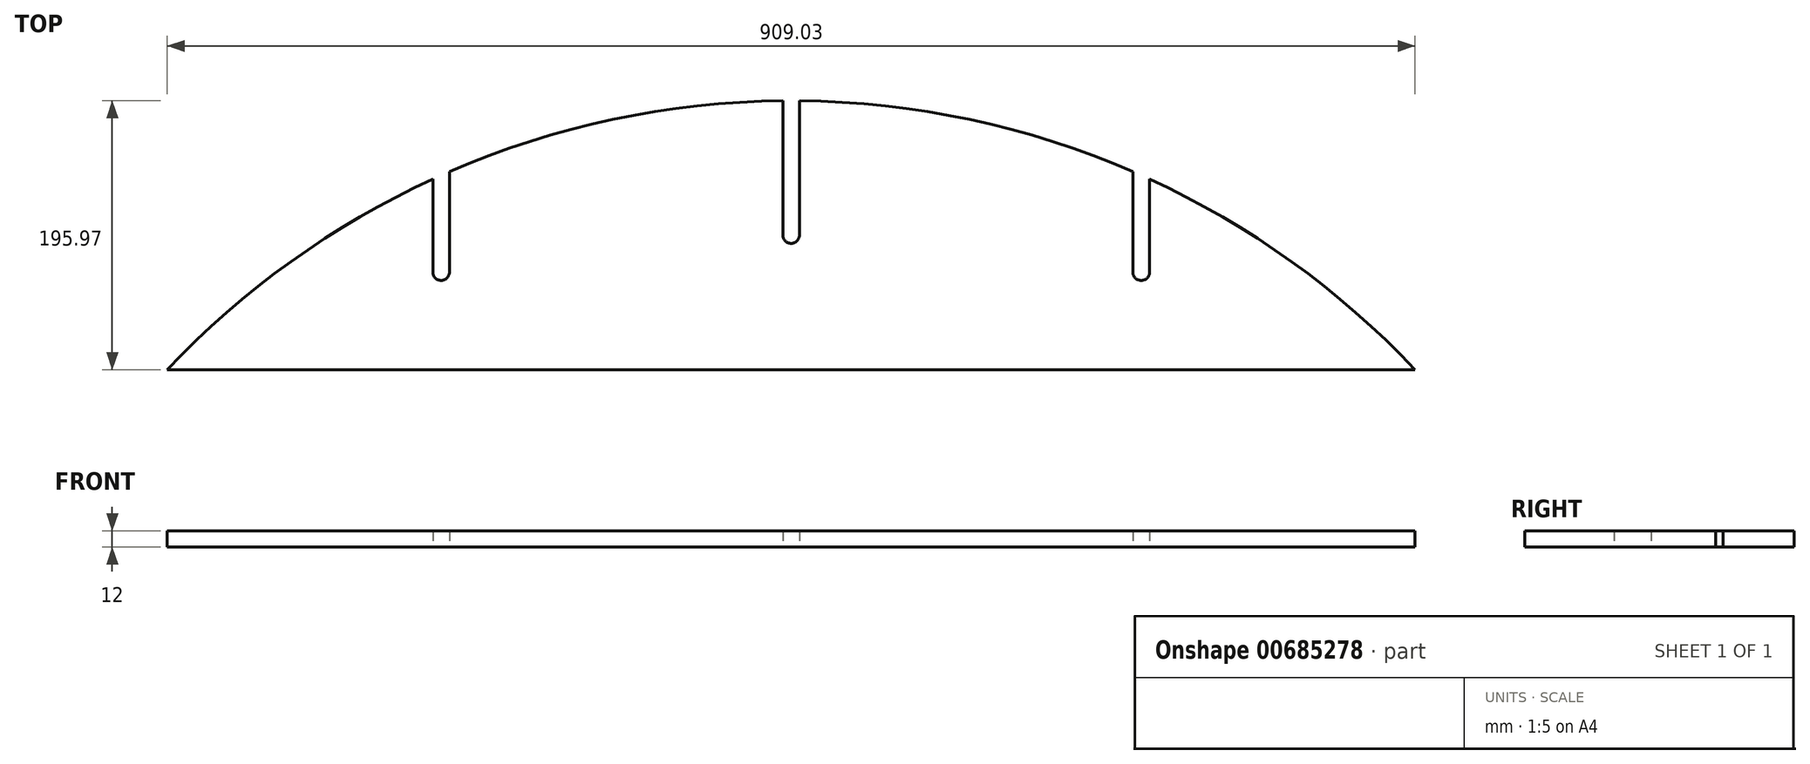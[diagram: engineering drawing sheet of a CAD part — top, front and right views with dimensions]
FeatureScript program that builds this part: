
annotation { "Feature Type Name" : "Feature", "Feature Type Description" : "" }
export const myFeature = defineFeature(function(context is Context, id is Id, definition is map)
    precondition{}
    {
        {
            var Q0;
            Q0=qCreatedBy(makeId("Top.planeOp"),FACE);
            var sketch = newSketch(context, id + "F0", { "sketchPlane" : qUnion([Q0])});
            skArc(sketch, "E0", {"start": v(909.03, 0) * mm, "mid": v(818.95, 78.75) * mm, "end": v(715.52, 138.9) * mm});
            skLineSegment(sketch, "E1", {"start": v(0, 0) * mm, "end": v(909.03, 0) * mm});
            skLineSegment(sketch, "E2", {"start": v(454.52, 252.18) * mm, "end": v(454.52, -138.83) * mm, "construction": true});
            skPoint(sketch, "E3", {"position": v(454.52, 0) * mm});
            skLineSegment(sketch, "E4", {"start": v(448.52, 195.97) * mm, "end": v(448.52, 98) * mm});
            skLineSegment(sketch, "E5", {"start": v(460.52, 98) * mm, "end": v(460.52, 195.97) * mm});
            skArc(sketch, "E6.trimOffspring", {"start": v(448.52, 195.97) * mm, "mid": v(324.42, 182.31) * mm, "end": v(205.52, 144.26) * mm});
            skLineSegment(sketch, "E7", {"start": v(199.52, 141.61) * mm, "end": v(199.52, -61.83) * mm, "construction": true});
            skLineSegment(sketch, "E8", {"start": v(193.52, 138.9) * mm, "end": v(193.52, 71) * mm});
            skLineSegment(sketch, "E9", {"start": v(205.52, 71) * mm, "end": v(205.52, 144.26) * mm});
            skLineSegment(sketch, "E10.MirrorCS", {"start": v(703.52, 71) * mm, "end": v(703.52, 144.26) * mm});
            skLineSegment(sketch, "E11.MirrorCS", {"start": v(715.52, 138.9) * mm, "end": v(715.52, 71) * mm});
            skArc(sketch, "E12.trimOffspring", {"start": v(703.52, 144.26) * mm, "mid": v(584.61, 182.31) * mm, "end": v(460.52, 195.97) * mm});
            skArc(sketch, "E13.trimOffspring", {"start": v(193.52, 138.9) * mm, "mid": v(90.08, 78.75) * mm, "end": v(0, 0) * mm});
            skArc(sketch, "E14", {"start": v(193.52, 71) * mm, "mid": v(199.52, 65) * mm, "end": v(205.52, 71) * mm});
            skArc(sketch, "E15", {"start": v(448.52, 98) * mm, "mid": v(454.52, 92) * mm, "end": v(460.52, 98) * mm});
            skArc(sketch, "E16", {"start": v(703.52, 71) * mm, "mid": v(709.52, 65) * mm, "end": v(715.52, 71) * mm});
            skSolve(sketch);
        }
        {
            var Q0;
            Q0=makeQuery(id+"F0.imprint","IMPRINT",FACE,{"disambiguationData":[TD([[makeQuery(id+"F0.imprint","IMPRINT",EDGE,{"derivedFrom":sQuery(id+"F0.wireOp",EDGE,"E0")}),1.0]])]});
            extrude(context, id + "F1", {"entities" : qUnion([Q0]), "depth" : 12 * mm, "offsetDistance" : 25 * mm});
        }
    });
